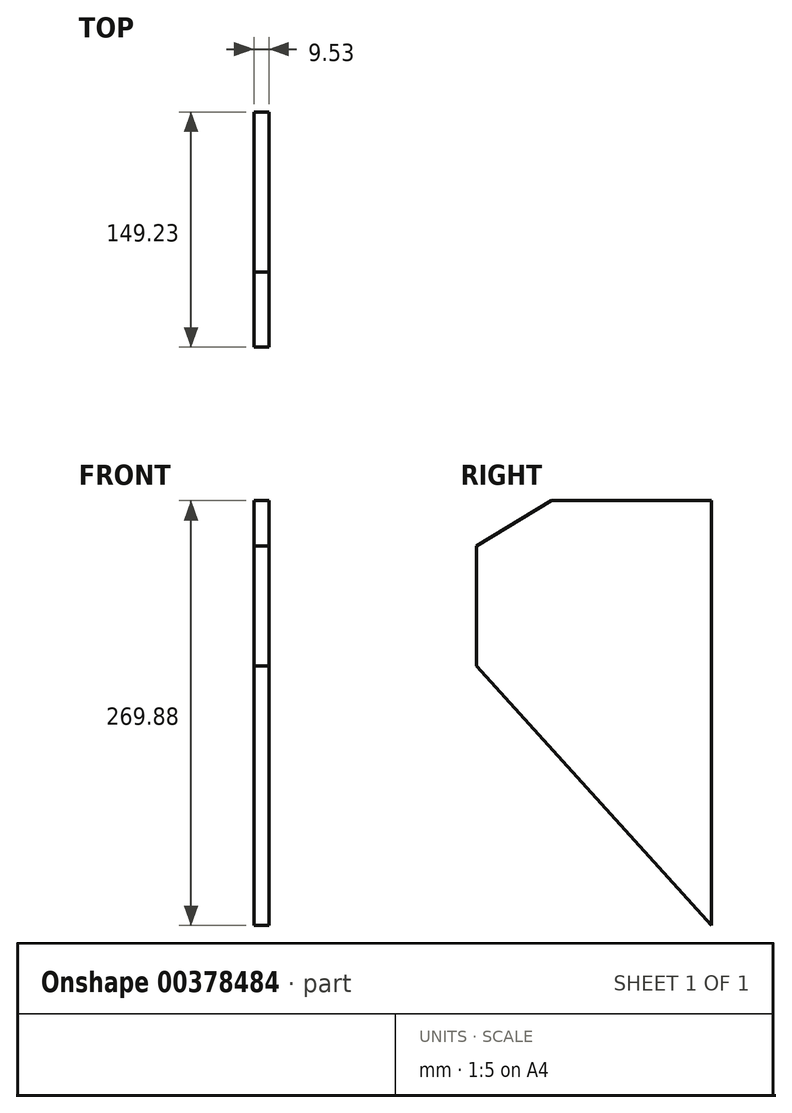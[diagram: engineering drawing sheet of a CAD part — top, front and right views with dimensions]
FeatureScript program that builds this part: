
annotation { "Feature Type Name" : "Feature", "Feature Type Description" : "" }
export const myFeature = defineFeature(function(context is Context, id is Id, definition is map)
    precondition{}
    {
        {
            var Q0;
            Q0=qCreatedBy(makeId("Right.planeOp"),FACE);
            var sketch = newSketch(context, id + "F0", { "sketchPlane" : qUnion([Q0])});
            skLineSegment(sketch, "E0", {"start": v(0, 0) * mm, "end": v(0, 269.88) * mm});
            skLineSegment(sketch, "E1", {"start": v(0, 269.88) * mm, "end": v(-101.6, 269.88) * mm});
            skLineSegment(sketch, "E2", {"start": v(-101.6, 269.88) * mm, "end": v(-149.23, 240.9) * mm});
            skLineSegment(sketch, "E3", {"start": v(-149.23, 240.9) * mm, "end": v(-149.23, 164.7) * mm});
            skLineSegment(sketch, "E4", {"start": v(-149.23, 164.7) * mm, "end": v(0, 0) * mm});
            skSolve(sketch);
        }
        {
            var Q0;
            Q0 = qSketchRegion(id + "F0", true);
            extrude(context, id + "F1", {"entities" : qUnion([Q0]), "depth" : 9.52 * mm});
        }
    });
